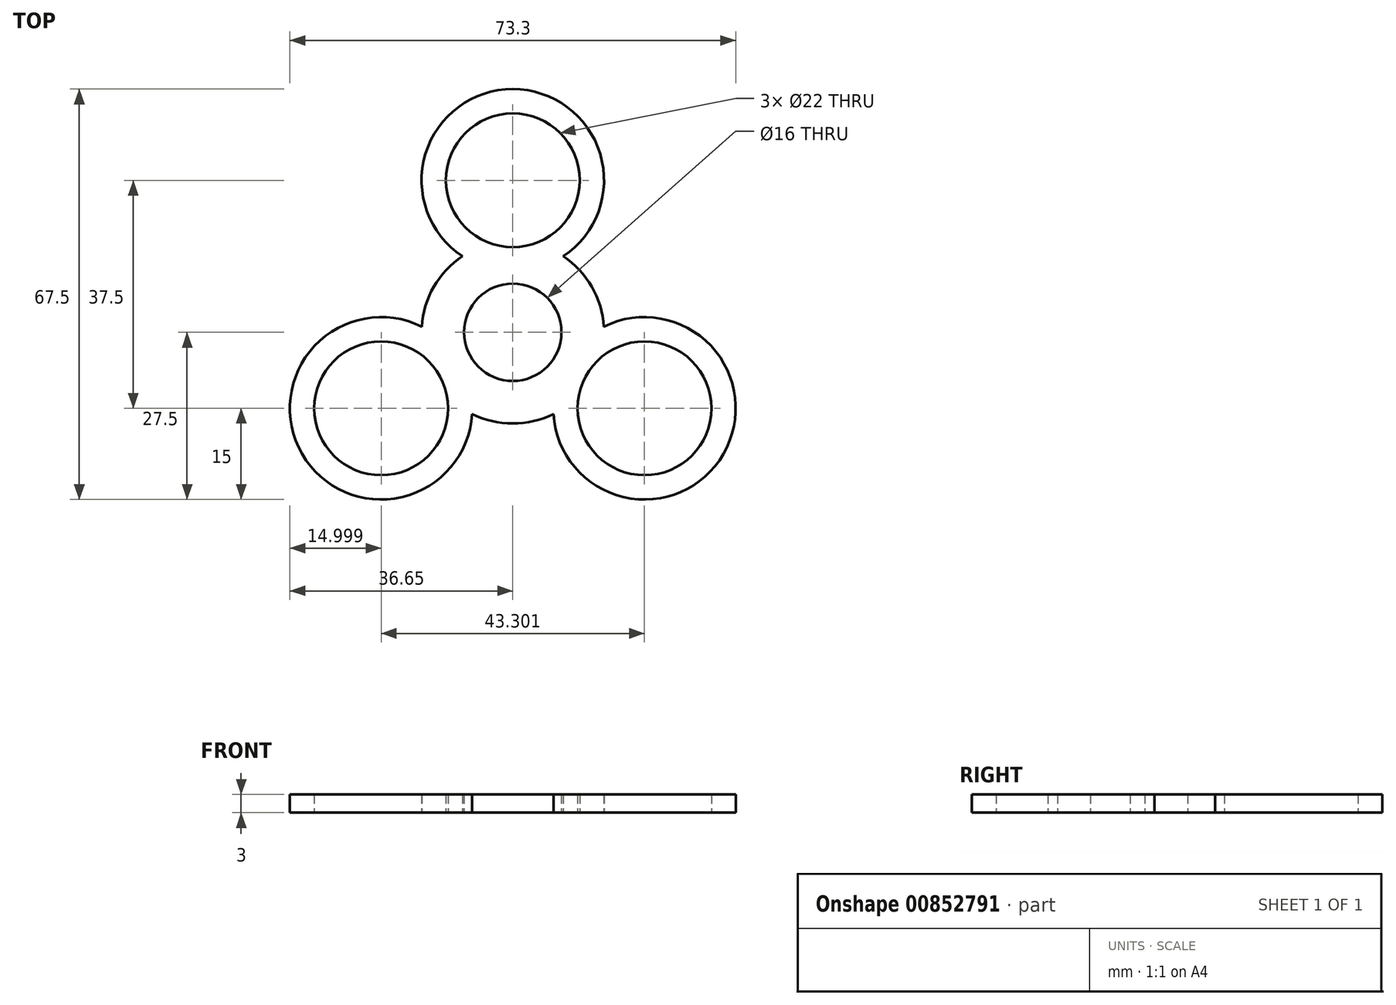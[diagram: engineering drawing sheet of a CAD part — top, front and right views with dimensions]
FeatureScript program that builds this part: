
annotation { "Feature Type Name" : "Feature", "Feature Type Description" : "" }
export const myFeature = defineFeature(function(context is Context, id is Id, definition is map)
    precondition{}
    {
        {
            var Q0;
            Q0=qCreatedBy(makeId("Top.planeOp"),FACE);
            var sketch = newSketch(context, id + "F0", { "sketchPlane" : qUnion([Q0])});
            skCircle(sketch, "E0", {"center": v(0, 0) * mm, "radius": 8 * mm});
            skArc(sketch, "E1", {"start": v(-8.3, 12.5) * mm, "mid": v(-13, 7.5) * mm, "end": v(-14.97, 0.93) * mm});
            skCircle(sketch, "E2", {"center": v(0, 25) * mm, "radius": 11 * mm});
            skArc(sketch, "E3", {"start": v(8.3, 12.5) * mm, "mid": v(0, 40) * mm, "end": v(-8.3, 12.5) * mm});
            skCircle(sketch, "E4.1.0", {"center": v(-21.65, -12.5) * mm, "radius": 11 * mm});
            skArc(sketch, "E4.1.1", {"start": v(-14.97, 0.93) * mm, "mid": v(-34.64, -20) * mm, "end": v(-6.68, -13.43) * mm});
            skCircle(sketch, "E4.2.0", {"center": v(21.65, -12.5) * mm, "radius": 11 * mm});
            skArc(sketch, "E4.2.1", {"start": v(6.68, -13.43) * mm, "mid": v(34.64, -20) * mm, "end": v(14.97, 0.93) * mm});
            skArc(sketch, "E5.trimOffspring", {"start": v(-6.68, -13.43) * mm, "mid": v(0, -15) * mm, "end": v(6.68, -13.43) * mm});
            skArc(sketch, "E6.trimOffspring", {"start": v(14.97, 0.93) * mm, "mid": v(13, 7.5) * mm, "end": v(8.3, 12.5) * mm});
            skSolve(sketch);
        }
        {
            var Q0;
            Q0=qSketchRegion(id+"F0",true);
            extrude(context, id + "F1", {"entities" : qUnion([Q0]), "depth" : 3 * mm, "offsetDistance" : 25 * mm});
        }
    });
